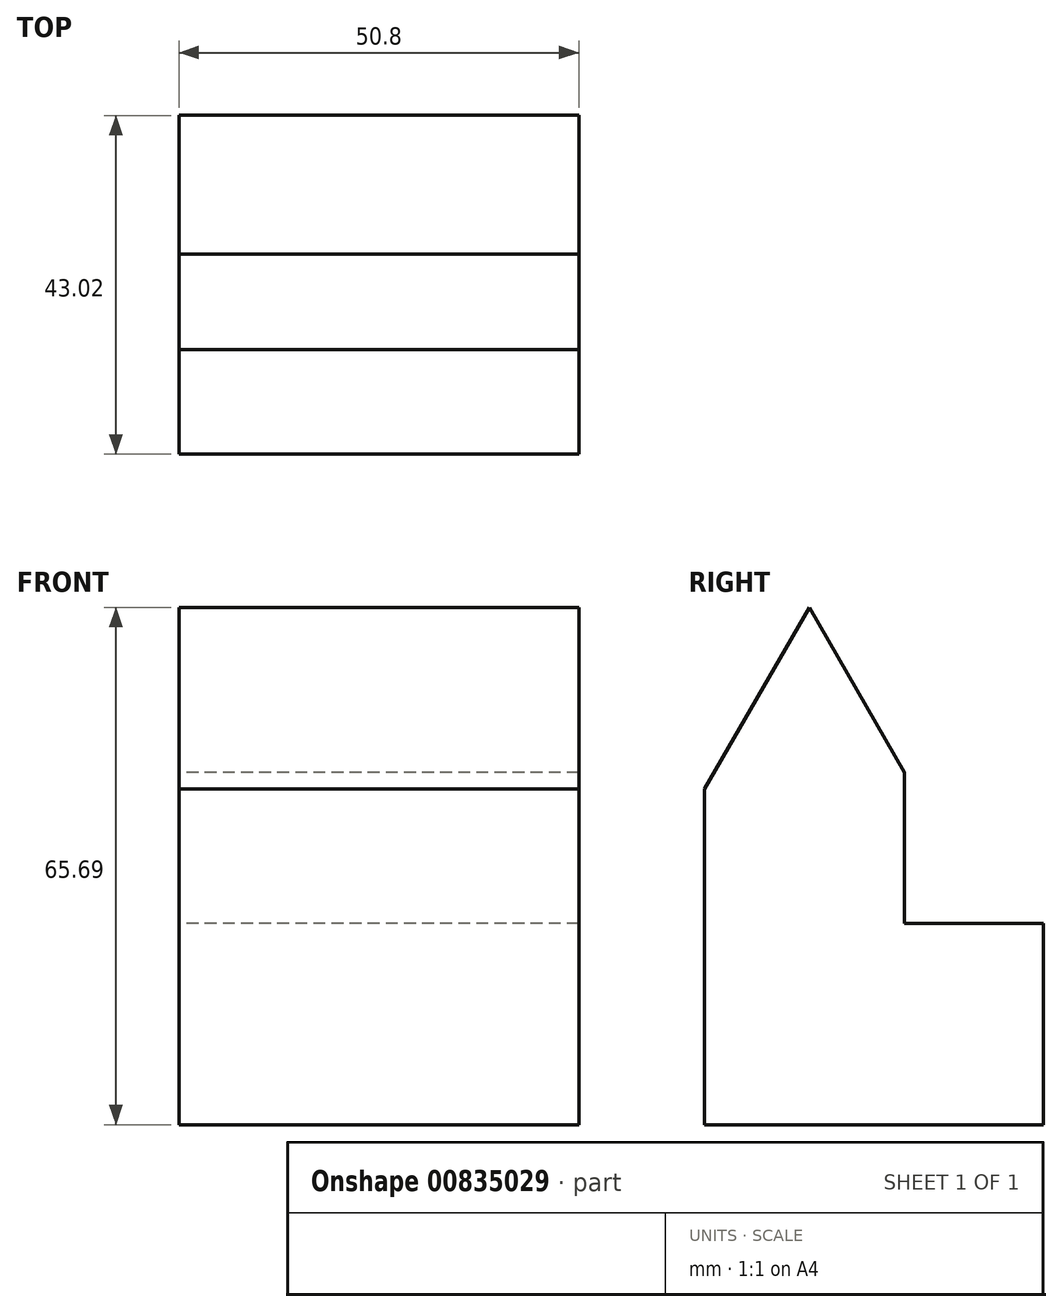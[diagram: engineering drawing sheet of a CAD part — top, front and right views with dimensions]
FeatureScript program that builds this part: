
annotation { "Feature Type Name" : "Feature", "Feature Type Description" : "" }
export const myFeature = defineFeature(function(context is Context, id is Id, definition is map)
    precondition{}
    {
        {
            var Q0;
            Q0=qCreatedBy(makeId("Right.planeOp"),FACE);
            var sketch = newSketch(context, id + "F0", { "sketchPlane" : qUnion([Q0])});
            skLineSegment(sketch, "E0", {"start": v(-9.25, 31.5) * mm, "end": v(-9.25, -11.16) * mm});
            skLineSegment(sketch, "E1", {"start": v(-9.25, -11.16) * mm, "end": v(33.77, -11.16) * mm});
            skLineSegment(sketch, "E2", {"start": v(33.77, -11.16) * mm, "end": v(33.77, 14.43) * mm});
            skLineSegment(sketch, "E3", {"start": v(33.77, 14.43) * mm, "end": v(16.15, 14.43) * mm});
            skLineSegment(sketch, "E4", {"start": v(16.15, 14.43) * mm, "end": v(16.15, 33.58) * mm});
            skLineSegment(sketch, "E5", {"start": v(16.15, 33.58) * mm, "end": v(4.05, 54.53) * mm});
            skLineSegment(sketch, "E6", {"start": v(4.05, 54.53) * mm, "end": v(-9.25, 31.5) * mm});
            skSolve(sketch);
        }
        {
            var Q0;
            Q0=makeQuery(id+"F0.imprint","IMPRINT",FACE,{"disambiguationData":[TD([[makeQuery(id+"F0.imprint","IMPRINT",EDGE,{"derivedFrom":sQuery(id+"F0.wireOp",EDGE,"E0")}),1.0]])]});
            extrude(context, id + "F1", {"entities" : qUnion([Q0]), "depth" : 50.8 * mm, "offsetDistance" : 25.4 * mm});
        }
    });
